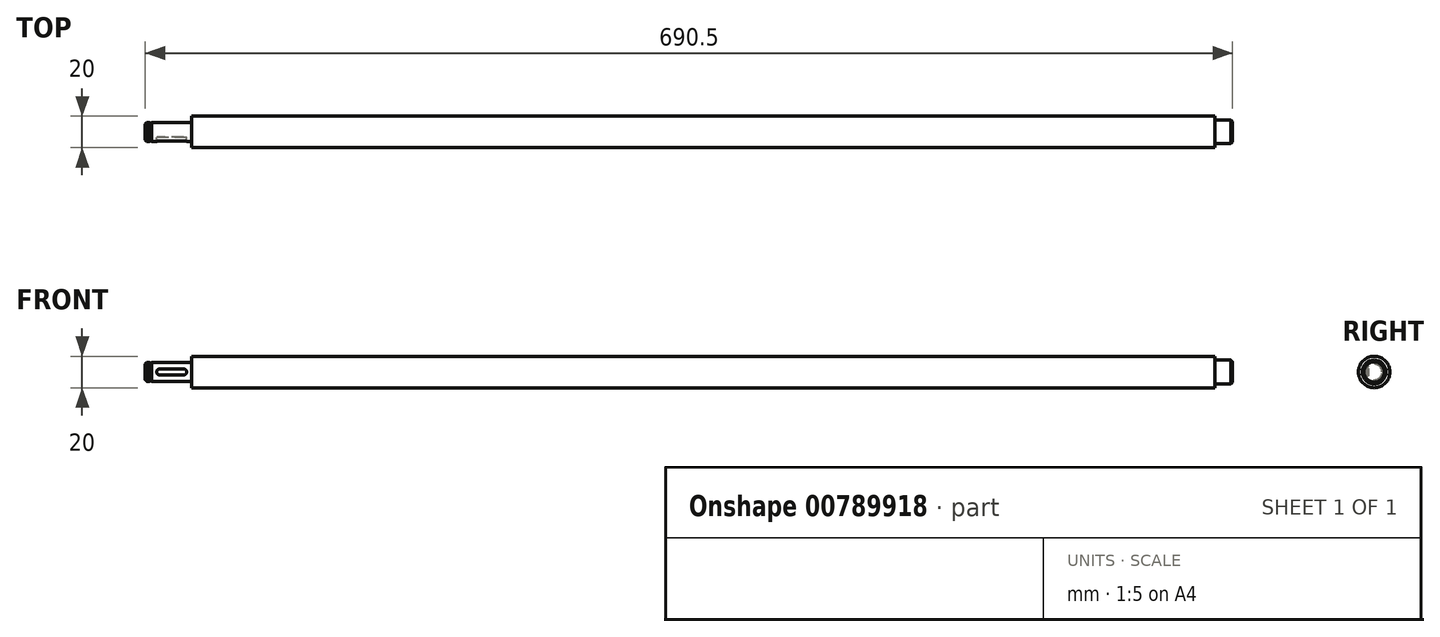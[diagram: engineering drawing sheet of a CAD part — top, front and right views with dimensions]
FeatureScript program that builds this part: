
annotation { "Feature Type Name" : "Feature", "Feature Type Description" : "" }
export const myFeature = defineFeature(function(context is Context, id is Id, definition is map)
    precondition{}
    {
        {
            var Q0;
            Q0=qCreatedBy(makeId("Front.planeOp"),FACE);
            var sketch = newSketch(context, id + "F0", { "sketchPlane" : qUnion([Q0])});
            skLineSegment(sketch, "E0", {"start": v(-345.25, 0) * mm, "end": v(345.25, 0) * mm});
            skLineSegment(sketch, "E1", {"start": v(345.25, 0) * mm, "end": v(345.25, 7.5) * mm});
            skLineSegment(sketch, "E2", {"start": v(345.25, 7.5) * mm, "end": v(334.25, 7.5) * mm});
            skLineSegment(sketch, "E3", {"start": v(334.25, 7.5) * mm, "end": v(334.25, 10) * mm});
            skLineSegment(sketch, "E4", {"start": v(334.25, 10) * mm, "end": v(-315.75, 10) * mm});
            skLineSegment(sketch, "E5", {"start": v(-315.75, 10) * mm, "end": v(-315.75, 6) * mm});
            skLineSegment(sketch, "E6", {"start": v(-315.75, 6) * mm, "end": v(-341.25, 6) * mm});
            skLineSegment(sketch, "E7", {"start": v(-345.25, 6) * mm, "end": v(-345.25, 0) * mm});
            skLineSegment(sketch, "E8", {"start": v(-341.25, 6) * mm, "end": v(-341.25, 5.75) * mm});
            skLineSegment(sketch, "E9", {"start": v(-341.25, 5.75) * mm, "end": v(-342.55, 5.75) * mm});
            skLineSegment(sketch, "E10", {"start": v(-342.55, 5.75) * mm, "end": v(-342.55, 6) * mm});
            skLineSegment(sketch, "E11", {"start": v(-342.55, 6) * mm, "end": v(-345.25, 6) * mm});
            skLineSegment(sketch, "E12", {"start": v(-448.42, 0) * mm, "end": v(539.1, 0) * mm, "construction": true});
            skSolve(sketch);
        }
        {
            var Q0;
            Q0=qSketchRegion(id+"F0",true);
            var Q1;
            Q1=sQuery(id+"F0.wireOp",EDGE,"E12");
            revolve(context, id + "F1", {"surfaceOperationType" : NewSurfaceOperationType.NEW, "entities" : qUnion([Q0]), "axis" : qUnion([Q1]), "revolveType" : RevolveType.FULL});
        }
        {
            var Q0;
            Q0=makeQuery(id+"F1.opRevolve","SWEPT_EDGE",EDGE,{"disambiguationData":[OSD([sQuery(id+"F0.wireOp",EDGE,"E7"),sQuery(id+"F0.wireOp",EDGE,"E11")])]});
            var Q1;
            Q1=makeQuery(id+"F1.opRevolve","SWEPT_EDGE",EDGE,{"disambiguationData":[OSD([sQuery(id+"F0.wireOp",EDGE,"E1"),sQuery(id+"F0.wireOp",EDGE,"E2")])]});
            chamfer(context, id + "F2", {"entities" : qUnion([Q0, Q1]), "width" : 1 * mm, "tangentPropagation" : true});
        }
        {
            var Q0;
            Q0=qCreatedBy(makeId("Front.planeOp"),FACE);
            var sketch = newSketch(context, id + "F3", { "sketchPlane" : qUnion([Q0])});
            skLineSegment(sketch, "E13.bottom", {"start": v(-336, 2) * mm, "end": v(-321, 2) * mm});
            skLineSegment(sketch, "E13.top", {"start": v(-336, -2) * mm, "end": v(-321, -2) * mm});
            skLineSegment(sketch, "E13.left", {"start": v(-336, 2) * mm, "end": v(-336, -2) * mm});
            skLineSegment(sketch, "E13.right", {"start": v(-321, 2) * mm, "end": v(-321, -2) * mm});
            skArc(sketch, "E14", {"start": v(-336, 2) * mm, "mid": v(-338, 0) * mm, "end": v(-336, -2) * mm});
            skArc(sketch, "E15", {"start": v(-321, -2) * mm, "mid": v(-319, 0) * mm, "end": v(-321, 2) * mm});
            skLineSegment(sketch, "E16", {"start": v(-341.25, 6) * mm, "end": v(-315.75, 6) * mm, "construction": true});
            skLineSegment(sketch, "E17", {"start": v(-315.75, -6) * mm, "end": v(-341.25, -6) * mm, "construction": true});
            skLineSegment(sketch, "E18", {"start": v(-328.5, 6) * mm, "end": v(-328.5, -6) * mm, "construction": true});
            skSolve(sketch);
        }
        {
            var Q0;
            Q0=qSketchRegion(id+"F3",true);
            var Q1;
            Q1=makeQuery(id+"F1.opRevolve","SWEPT_FACE",FACE,{"disambiguationData":[OSD([sQuery(id+"F0.wireOp",EDGE,"E6")])]});
            extrude(context, id + "F4", {"entities" : qUnion([Q0]), "operationType" : NewBodyOperationType.REMOVE, "depth" : 10 * mm, "offsetDistance" : 2 * mm, "offsetOppositeDirection" : true, "hasSecondDirection" : true, "secondDirectionBound" : BoundingType.UP_TO_SURFACE, "secondDirectionOppositeDirection" : false, "secondDirectionDepth" : 5.3 * mm, "secondDirectionBoundEntityFace" : qUnion([Q1]), "hasSecondDirectionOffset" : true, "secondDirectionOffsetDistance" : 2.5 * mm});
        }
    });
